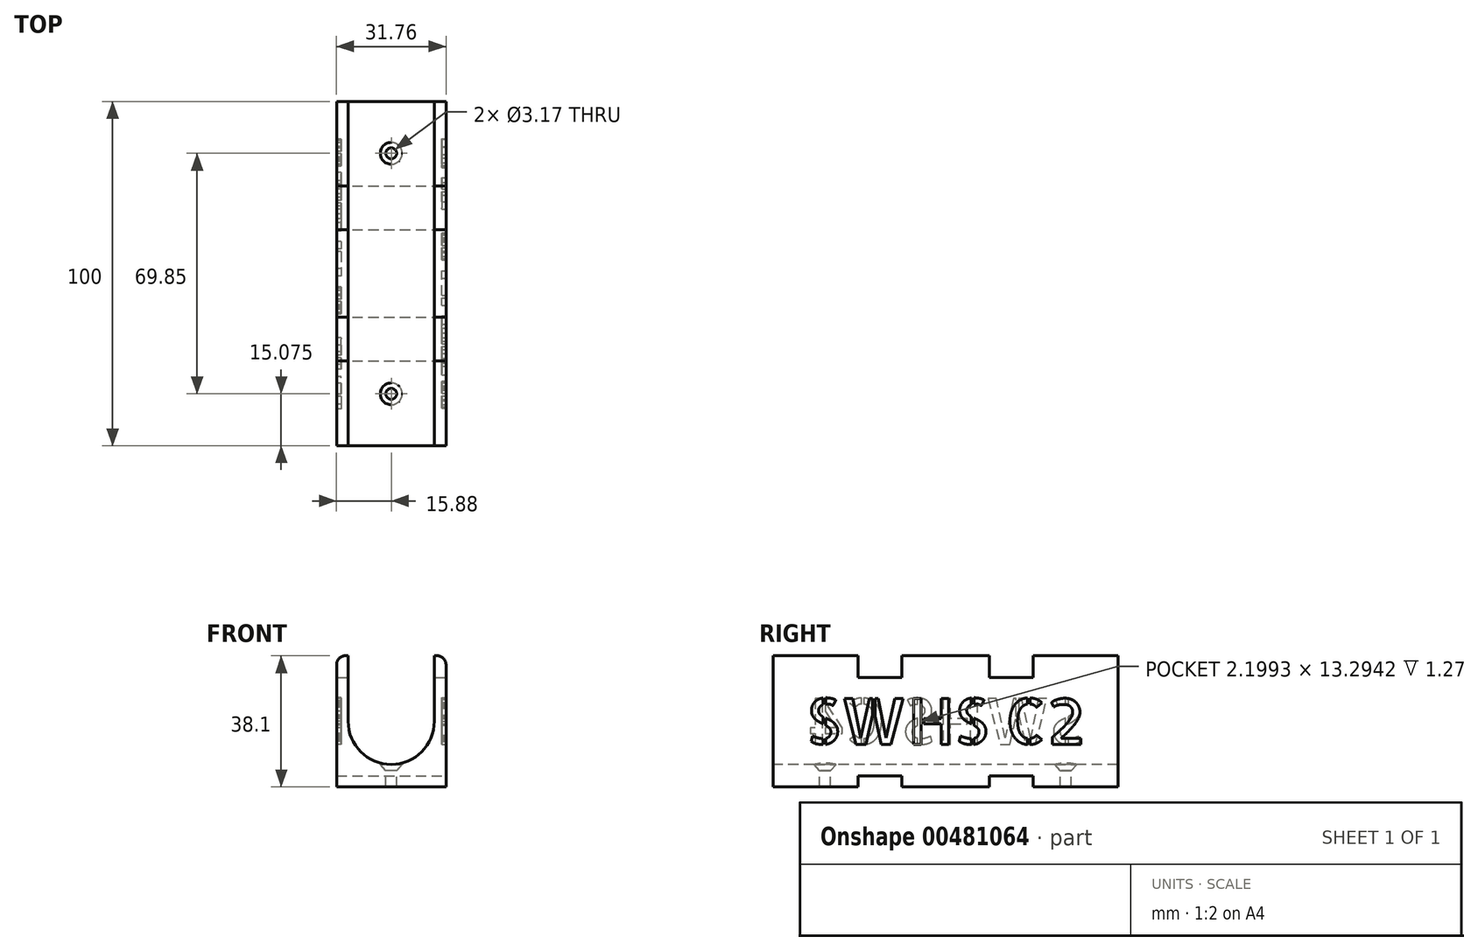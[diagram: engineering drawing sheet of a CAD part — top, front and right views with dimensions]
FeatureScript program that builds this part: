
annotation { "Feature Type Name" : "Feature", "Feature Type Description" : "" }
export const myFeature = defineFeature(function(context is Context, id is Id, definition is map)
    precondition{}
    {
        {
            var Q0;
            Q0=qCreatedBy(makeId("Front.planeOp"),FACE);
            var sketch = newSketch(context, id + "F0", { "sketchPlane" : qUnion([Q0])});
            skLineSegment(sketch, "E0.bottom", {"start": v(-15.87, 19.05) * mm, "end": v(-12.5, 19.05) * mm});
            skLineSegment(sketch, "E0.top", {"start": v(-15.88, -19.05) * mm, "end": v(15.87, -19.05) * mm});
            skLineSegment(sketch, "E0.left", {"start": v(-15.87, 19.05) * mm, "end": v(-15.88, -19.05) * mm});
            skLineSegment(sketch, "E0.right", {"start": v(15.88, 19.05) * mm, "end": v(15.87, -19.05) * mm});
            skPoint(sketch, "E0.middle", {"position": v(0, 0) * mm});
            skArc(sketch, "E1", {"start": v(12.5, 0) * mm, "mid": v(0, -12.5) * mm, "end": v(-12.5, 0) * mm});
            skLineSegment(sketch, "E2", {"start": v(-12.5, 0) * mm, "end": v(-12.5, 19.05) * mm});
            skLineSegment(sketch, "E3", {"start": v(12.5, 0) * mm, "end": v(12.5, 19.05) * mm});
            skLineSegment(sketch, "E4.trimOffspring", {"start": v(12.5, 19.05) * mm, "end": v(15.88, 19.05) * mm});
            skSolve(sketch);
        }
        {
            var Q0;
            Q0=makeQuery(id+"F0.imprint","IMPRINT",FACE,{"disambiguationData":[TD([[makeQuery(id+"F0.imprint","IMPRINT",EDGE,{"derivedFrom":sQuery(id+"F0.wireOp",EDGE,"E0.bottom")}),-1.0]])]});
            extrude(context, id + "F1", {"entities" : qUnion([Q0]), "endBound" : BoundingType.SYMMETRIC, "oppositeDirection" : true, "depth" : 100 * mm});
        }
        {
            var Q0;
            Q0=makeQuery(id+"F1.opExtrude","SWEPT_FACE",FACE,{"disambiguationData":[OSD([sQuery(id+"F0.wireOp",EDGE,"E0.right")])]});
            var sketch = newSketch(context, id + "F2", { "sketchPlane" : qUnion([Q0])});
            skLineSegment(sketch, "E5.bottom", {"start": v(-25.4, -19.05) * mm, "end": v(-12.7, -19.05) * mm});
            skLineSegment(sketch, "E5.top", {"start": v(-25.4, -15.87) * mm, "end": v(-12.7, -15.87) * mm});
            skLineSegment(sketch, "E5.left", {"start": v(-25.4, -19.05) * mm, "end": v(-25.4, -15.87) * mm});
            skLineSegment(sketch, "E5.right", {"start": v(-12.7, -19.05) * mm, "end": v(-12.7, -15.87) * mm});
            skLineSegment(sketch, "E6.MirrorCS", {"start": v(25.4, -15.87) * mm, "end": v(12.7, -15.88) * mm});
            skLineSegment(sketch, "E7.MirrorCS", {"start": v(25.4, -19.05) * mm, "end": v(25.4, -15.87) * mm});
            skLineSegment(sketch, "E8.MirrorCS", {"start": v(12.7, -19.05) * mm, "end": v(12.7, -15.87) * mm});
            skLineSegment(sketch, "E9.MirrorCS", {"start": v(25.4, -19.05) * mm, "end": v(12.7, -19.05) * mm});
            skPoint(sketch, "E10", {"position": v(-12.7, 19.05) * mm});
            skPoint(sketch, "E11", {"position": v(-25.4, 19.05) * mm});
            skPoint(sketch, "E12", {"position": v(12.7, 19.05) * mm});
            skPoint(sketch, "E12.positionSnap0", {"position": v(0, 19.05) * mm});
            skPoint(sketch, "E13", {"position": v(25.4, 19.05) * mm});
            skLineSegment(sketch, "E14.bottom", {"start": v(-25.4, 19.05) * mm, "end": v(-12.7, 19.05) * mm});
            skLineSegment(sketch, "E14.top", {"start": v(-25.4, 12.7) * mm, "end": v(-12.7, 12.7) * mm});
            skLineSegment(sketch, "E14.left", {"start": v(-25.4, 19.05) * mm, "end": v(-25.4, 12.7) * mm});
            skLineSegment(sketch, "E14.right", {"start": v(-12.7, 19.05) * mm, "end": v(-12.7, 12.7) * mm});
            skLineSegment(sketch, "E15.MirrorCS", {"start": v(12.7, 19.05) * mm, "end": v(12.7, 12.7) * mm});
            skLineSegment(sketch, "E16.MirrorCS", {"start": v(25.4, 12.7) * mm, "end": v(12.7, 12.7) * mm});
            skLineSegment(sketch, "E17.MirrorCS", {"start": v(25.4, 19.05) * mm, "end": v(25.4, 12.7) * mm});
            skLineSegment(sketch, "E18.MirrorCS", {"start": v(25.4, 19.05) * mm, "end": v(12.7, 19.05) * mm});
            skSolve(sketch);
        }
        {
            var Q0;
            Q0=makeQuery(id+"F2.imprint","IMPRINT",FACE,{"disambiguationData":[TD([[makeQuery(id+"F2.imprint","IMPRINT",EDGE,{"derivedFrom":sQuery(id+"F2.wireOp",EDGE,"E5.bottom")}),-1.0]])]});
            var Q1;
            Q1=makeQuery(id+"F2.imprint","IMPRINT",FACE,{"disambiguationData":[TD([[makeQuery(id+"F2.imprint","IMPRINT",EDGE,{"derivedFrom":sQuery(id+"F2.wireOp",EDGE,"E6.MirrorCS")}),1.0]])]});
            extrude(context, id + "F3", {"entities" : qUnion([Q0, Q1]), "operationType" : NewBodyOperationType.REMOVE, "endBound" : BoundingType.THROUGH_ALL, "oppositeDirection" : true, "depth" : 25.4 * mm});
        }
        {
            var Q0;
            Q0=makeQuery(id+"F1.opExtrude","CAP_EDGE",EDGE,{"disambiguationData":[OSD([sQuery(id+"F0.wireOp",EDGE,"E1")])],"isStart":false});
            cPoint(context, id + "F4", {"entities" : qUnion([Q0]), "parameter" : 0.5});
        }
        {
            var Q0;
            Q0 = qCreatedBy(id + "F4" ,VERTEX);
            var Q1;
            Q1=qCreatedBy(makeId("Top.planeOp"),FACE);
            cPlane(context, id + "F5", {"entities" : qUnion([Q0, Q1]), "cplaneType" : CPlaneType.PLANE_POINT, "offset" : 25.4 * mm, "width" : 152.4 * mm, "height" : 152.4 * mm});
        }
        {
            var Q0;
            Q0=qCreatedBy(id+"F5.planeOp",FACE);
            var sketch = newSketch(context, id + "F6", { "sketchPlane" : qUnion([Q0])});
            skPoint(sketch, "E19", {"position": v(0, 34.93) * mm});
            skPoint(sketch, "E20.MirrorP", {"position": v(0, -34.93) * mm});
            skSolve(sketch);
        }
        {
            var Q0;
            Q0=sQuery(id+"F6.wireOp",VERTEX,"E19");
            var Q1;
            Q1=sQuery(id+"F6.wireOp",VERTEX,"E20.MirrorP");
            var Q2;
            Q2=makeQuery(id+"F1.opExtrude","SWEPT_BODY",BODY,{"disambiguationData":[OSD([sQuery(id+"F0.wireOp",EDGE,"E0.bottom"),sQuery(id+"F0.wireOp",EDGE,"E0.top"),sQuery(id+"F0.wireOp",EDGE,"E0.left"),sQuery(id+"F0.wireOp",EDGE,"E0.right"),sQuery(id+"F0.wireOp",EDGE,"E1"),sQuery(id+"F0.wireOp",EDGE,"E2"),sQuery(id+"F0.wireOp",EDGE,"E3"),sQuery(id+"F0.wireOp",EDGE,"E4.trimOffspring")])]});
            hole(context, id + "F7", {"style" : HoleStyle.SIMPLE, "endStyle" : HoleEndStyle.THROUGH, "oppositeDirection" : true, "holeDiameter" : 6.35 * mm, "isTappedThrough" : true, "tappedDepth" : 12.7 * mm, "tapClearance" : 3, "startFromSketch" : true, "locations" : qUnion([Q0, Q1]), "scope" : qUnion([Q2])});
        }
        {
            var Q0;
            Q0=sQuery(id+"F6.wireOp",VERTEX,"E19");
            var Q1;
            Q1=sQuery(id+"F6.wireOp",VERTEX,"E20.MirrorP");
            var Q2;
            Q2=makeQuery(id+"F1.opExtrude","SWEPT_BODY",BODY,{"disambiguationData":[OSD([sQuery(id+"F0.wireOp",EDGE,"E0.bottom"),sQuery(id+"F0.wireOp",EDGE,"E0.top"),sQuery(id+"F0.wireOp",EDGE,"E0.left"),sQuery(id+"F0.wireOp",EDGE,"E0.right"),sQuery(id+"F0.wireOp",EDGE,"E1"),sQuery(id+"F0.wireOp",EDGE,"E2"),sQuery(id+"F0.wireOp",EDGE,"E3"),sQuery(id+"F0.wireOp",EDGE,"E4.trimOffspring")])]});
            hole(context, id + "F8", {"style" : HoleStyle.C_SINK, "endStyle" : HoleEndStyle.THROUGH, "holeDiameter" : 3.17 * mm, "cSinkDiameter" : 6.35 * mm, "cSinkAngle" : 82 * degree, "isTappedThrough" : true, "tappedDepth" : 12.7 * mm, "tapClearance" : 3, "startFromSketch" : true, "locations" : qUnion([Q0, Q1]), "scope" : qUnion([Q2])});
        }
        {
            var Q0;
            {var subQ0=sQuery(id+"F0.wireOp",EDGE,"E4.trimOffspring");var subQ1=sQuery(id+"F0.wireOp",EDGE,"E0.right");Q0=makeQuery(id+"FeQ3rhoPdLxqioT_1.boolean.opBoolean","SPLIT",EDGE,{"disambiguationData":[TD([makeQuery(id+"FeQ3rhoPdLxqioT_1.opExtrude","SWEPT_FACE",FACE,{"disambiguationData":[OSD([sQuery(id+"F2.wireOp",EDGE,"E17.MirrorCS")])]})])],"derivedFrom":makeQuery(id+"F1.opExtrude","SWEPT_EDGE",EDGE,{"disambiguationData":[OSD([subQ1,subQ0])]})});}
            var Q1;
            {var subQ0=sQuery(id+"F0.wireOp",EDGE,"E0.right");var subQ1=sQuery(id+"F0.wireOp",EDGE,"E4.trimOffspring");Q1=makeQuery(id+"FeQ3rhoPdLxqioT_1.boolean.opBoolean","SPLIT",EDGE,{"disambiguationData":[TD([makeQuery(id+"FeQ3rhoPdLxqioT_1.opExtrude","SWEPT_FACE",FACE,{"disambiguationData":[OSD([sQuery(id+"F2.wireOp",EDGE,"E14.right")])]})])],"derivedFrom":makeQuery(id+"F1.opExtrude","SWEPT_EDGE",EDGE,{"disambiguationData":[OSD([subQ0,subQ1])]})});}
            var Q2;
            {var subQ0=sQuery(id+"F0.wireOp",EDGE,"E4.trimOffspring");var subQ1=sQuery(id+"F0.wireOp",EDGE,"E0.right");Q2=makeQuery(id+"FeQ3rhoPdLxqioT_1.boolean.opBoolean","SPLIT",EDGE,{"disambiguationData":[TD([makeQuery(id+"FeQ3rhoPdLxqioT_1.opExtrude","SWEPT_FACE",FACE,{"disambiguationData":[OSD([sQuery(id+"F2.wireOp",EDGE,"E14.left")])]})])],"derivedFrom":makeQuery(id+"F1.opExtrude","SWEPT_EDGE",EDGE,{"disambiguationData":[OSD([subQ1,subQ0])]})});}
            var Q3;
            {var subQ0=sQuery(id+"F0.wireOp",EDGE,"E0.bottom");var subQ1=sQuery(id+"F0.wireOp",EDGE,"E0.left");Q3=makeQuery(id+"FeQ3rhoPdLxqioT_1.boolean.opBoolean","SPLIT",EDGE,{"disambiguationData":[TD([makeQuery(id+"FeQ3rhoPdLxqioT_1.opExtrude","SWEPT_FACE",FACE,{"disambiguationData":[OSD([sQuery(id+"F2.wireOp",EDGE,"E14.left")])]})])],"derivedFrom":makeQuery(id+"F1.opExtrude","SWEPT_EDGE",EDGE,{"disambiguationData":[OSD([subQ0,subQ1])]})});}
            var Q4;
            {var subQ0=sQuery(id+"F0.wireOp",EDGE,"E0.bottom");var subQ1=sQuery(id+"F0.wireOp",EDGE,"E0.left");Q4=makeQuery(id+"FeQ3rhoPdLxqioT_1.boolean.opBoolean","SPLIT",EDGE,{"disambiguationData":[TD([makeQuery(id+"FeQ3rhoPdLxqioT_1.opExtrude","SWEPT_FACE",FACE,{"disambiguationData":[OSD([sQuery(id+"F2.wireOp",EDGE,"E14.right")])]})])],"derivedFrom":makeQuery(id+"F1.opExtrude","SWEPT_EDGE",EDGE,{"disambiguationData":[OSD([subQ0,subQ1])]})});}
            var Q5;
            {var subQ0=sQuery(id+"F0.wireOp",EDGE,"E0.bottom");var subQ1=sQuery(id+"F0.wireOp",EDGE,"E0.left");Q5=makeQuery(id+"FeQ3rhoPdLxqioT_1.boolean.opBoolean","SPLIT",EDGE,{"disambiguationData":[TD([makeQuery(id+"FeQ3rhoPdLxqioT_1.opExtrude","SWEPT_FACE",FACE,{"disambiguationData":[OSD([sQuery(id+"F2.wireOp",EDGE,"E17.MirrorCS")])]})])],"derivedFrom":makeQuery(id+"F1.opExtrude","SWEPT_EDGE",EDGE,{"disambiguationData":[OSD([subQ0,subQ1])]})});}
            fillet(context, id + "F9", {"entities" : qUnion([Q0, Q1, Q2, Q3, Q4, Q5]), "radius" : 2.54 * mm, "tangentPropagation" : true, "allowEdgeOverflow" : false});
        }
        {
            var Q0;
            Q0=makeQuery(id+"F2.imprint","IMPRINT",FACE,{"disambiguationData":[TD([[makeQuery(id+"F2.imprint","IMPRINT",EDGE,{"derivedFrom":sQuery(id+"F2.wireOp",EDGE,"E5.top")}),1.0]])]});
            var sketch = newSketch(context, id + "F10", { "sketchPlane" : qUnion([Q0])});
            skText(sketch, "E21", { "text": "SWHS C2", "fontName": "AllertaStencil-Regular.ttf"});
            const initialGuessF10  = {"E21": [-0.04047, -0.00665, 1, 0, 0.0133]};
            skSetInitialGuess(sketch, initialGuessF10);
            skSolve(sketch);
        }
        {
            var Q0;
            Q0 = qSketchRegion(id + "F10", true);
            extrude(context, id + "F11", {"entities" : qUnion([Q0]), "operationType" : NewBodyOperationType.REMOVE, "oppositeDirection" : true, "depth" : 1.27 * mm});
        }
        {
            var Q0;
            Q0=makeQuery(id+"F1.opExtrude","SWEPT_FACE",FACE,{"disambiguationData":[OSD([sQuery(id+"F0.wireOp",EDGE,"E0.left")])]});
            var sketch = newSketch(context, id + "F12", { "sketchPlane" : qUnion([Q0])});
            skText(sketch, "E22", { "text": "SWHS C4", "fontName": "AllertaStencil-Regular.ttf"});
            const initialGuessF12  = {"E22": [-0.04048, -0.00664, 1, 0, 0.01328]};
            skSetInitialGuess(sketch, initialGuessF12);
            skSolve(sketch);
        }
        {
            var Q0;
            Q0 = qSketchRegion(id + "F12", true);
            extrude(context, id + "F13", {"entities" : qUnion([Q0]), "operationType" : NewBodyOperationType.REMOVE, "oppositeDirection" : true, "depth" : 1.27 * mm});
        }
        {
            var Q0;
            Q0=makeQuery(id+"F2.imprint","IMPRINT",FACE,{"disambiguationData":[TD([[makeQuery(id+"F2.imprint","IMPRINT",EDGE,{"derivedFrom":sQuery(id+"F2.wireOp",EDGE,"E14.bottom")}),1.0]])]});
            var Q1;
            Q1=makeQuery(id+"F2.imprint","IMPRINT",FACE,{"disambiguationData":[TD([[makeQuery(id+"F2.imprint","IMPRINT",EDGE,{"derivedFrom":sQuery(id+"F2.wireOp",EDGE,"E15.MirrorCS")}),1.0]])]});
            extrude(context, id + "F14", {"entities" : qUnion([Q0, Q1]), "operationType" : NewBodyOperationType.REMOVE, "endBound" : BoundingType.THROUGH_ALL, "oppositeDirection" : true, "depth" : 25.4 * mm});
        }
    });
